# Revit family: OVEN_KITCHEN_SUBZERO_DO3050TE-S-TH
name_source: partatom
category: Specialty Equipment
revit_build: Autodesk Revit 2015 (Build: 20140606_1530(x64)
units: mm (PartAtom-declared; Revit-internal decimal feet)

## types (1)
- DO3050TE/S/TH
    Control panel material = Glass
    Cost = 4249 $
    Description = 30" SERIES TRANSITIONAL BUILT - IN DOUBLE OVEN
    Dimensions (WxHxD) (inches) = 29 7/8" x 50 3/8" x 23 3/4"
    Door clearance = 22"
    Door material = Glass
    Electrical service = 50 amp dedicated circuit
    Electrical supply = 240/208 VAC, 60 HZ
    Length electrical supply cord (feed) = 5
    Manufacturer = Subzero
    Model = DO3050TE/S/TH
    Oven 1 interior dimensions (WxHxD) (inches) = 25" x 16 1/2" x 19"
    Oven 2 interior dimensions (HxWxD) (inches) = 25" x 16 1/2" x 19"
    Overall capacity = 4.5 cu. ft.
    URL = https://www.subzero-wolf.com
    Usable capacity = 2.8 cu. ft.
    Usable volume of cavity (l) = 71

## geometry (parser evidence)
native form markers: Blend x2, Sweep x2
no freeform markers — native parametric forms only
